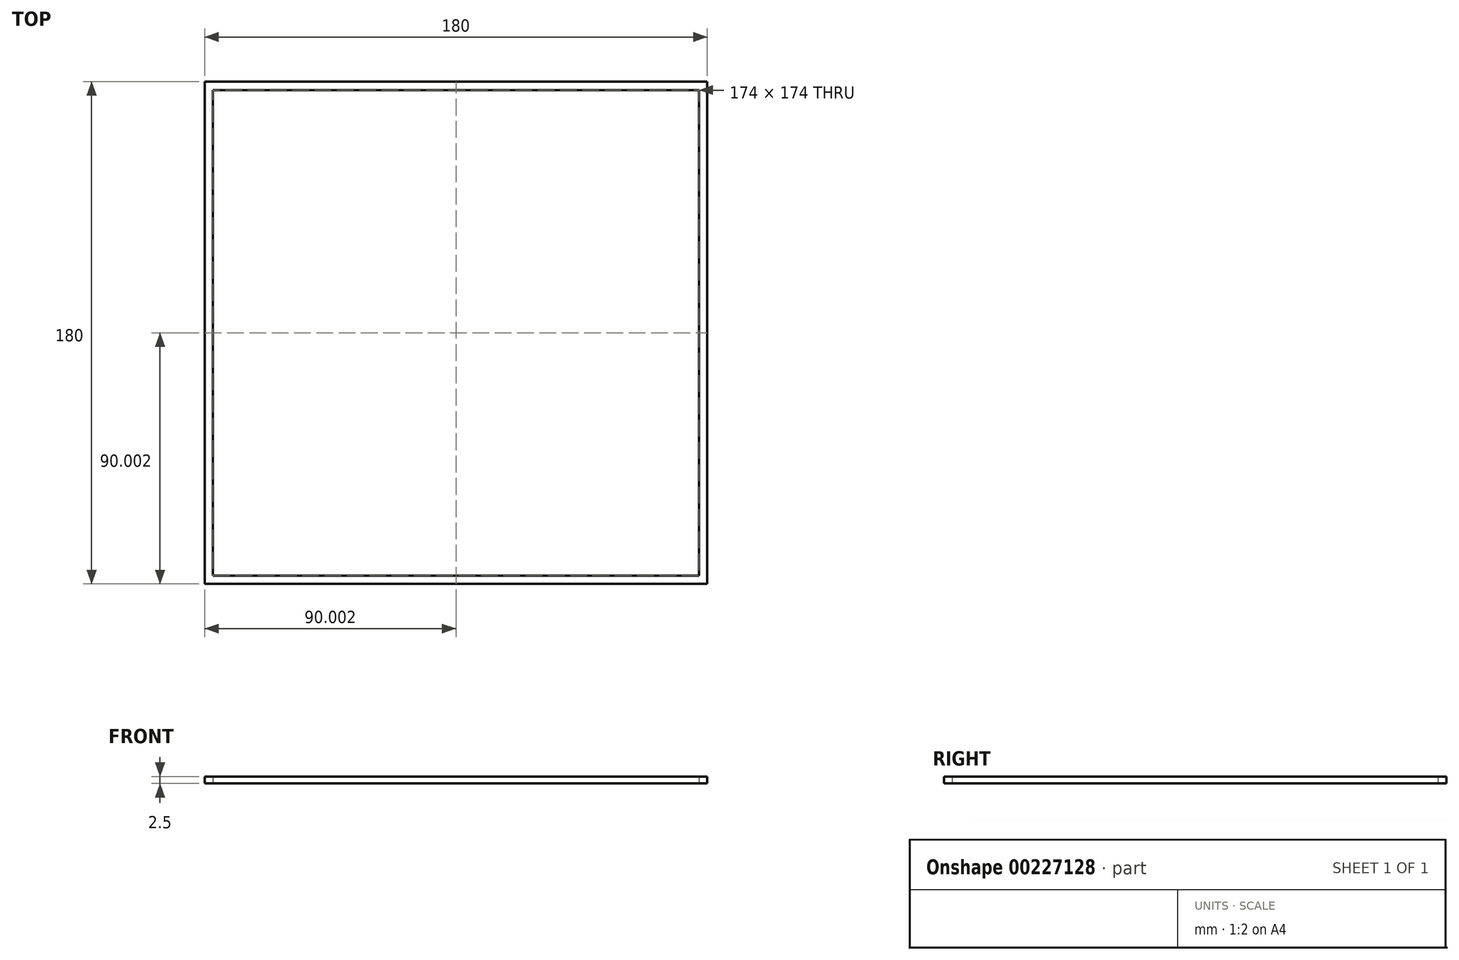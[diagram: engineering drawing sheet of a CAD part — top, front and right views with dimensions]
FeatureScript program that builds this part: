
annotation { "Feature Type Name" : "Feature", "Feature Type Description" : "" }
export const myFeature = defineFeature(function(context is Context, id is Id, definition is map)
    precondition{}
    {
        {
            var Q0;
            Q0=qCreatedBy(makeId("Top.planeOp"),FACE);
            var sketch = newSketch(context, id + "F0", { "sketchPlane" : qUnion([Q0])});
            skLineSegment(sketch, "E0.bottom", {"start": v(-160.02, 92.55) * mm, "end": v(19.98, 92.55) * mm});
            skLineSegment(sketch, "E0.top", {"start": v(-160.02, -87.45) * mm, "end": v(19.98, -87.45) * mm});
            skLineSegment(sketch, "E0.left", {"start": v(-160.02, 92.55) * mm, "end": v(-160.02, -87.45) * mm});
            skLineSegment(sketch, "E0.right", {"start": v(19.98, 92.55) * mm, "end": v(19.98, -87.45) * mm});
            skLineSegment(sketch, "E1.0", {"start": v(-157.02, 89.55) * mm, "end": v(-157.02, -84.45) * mm});
            skLineSegment(sketch, "E1.1", {"start": v(-157.02, 89.55) * mm, "end": v(16.98, 89.55) * mm});
            skLineSegment(sketch, "E1.2", {"start": v(16.98, 89.55) * mm, "end": v(16.98, -84.45) * mm});
            skLineSegment(sketch, "E1.3", {"start": v(-157.02, -84.45) * mm, "end": v(16.98, -84.45) * mm});
            skSolve(sketch);
        }
        {
            var Q0;
            Q0=makeQuery(id+"F0.imprint","IMPRINT",FACE,{"disambiguationData":[TD([[makeQuery(id+"F0.imprint","IMPRINT",EDGE,{"derivedFrom":sQuery(id+"F0.wireOp",EDGE,"E0.bottom")}),-1.0]])]});
            extrude(context, id + "F1", {"entities" : qUnion([Q0]), "depth" : 2.5 * mm});
        }
        {
            var Q0;
            Q0=makeQuery(id+"F0.imprint","IMPRINT",FACE,{"disambiguationData":[TD([[makeQuery(id+"F0.imprint","IMPRINT",EDGE,{"derivedFrom":sQuery(id+"F0.wireOp",EDGE,"E1.0")}),1.0]])]});
            extrude(context, id + "F2", {"entities" : qUnion([Q0]), "operationType" : NewBodyOperationType.REMOVE, "oppositeDirection" : true, "depth" : 25 * mm});
        }
    });
